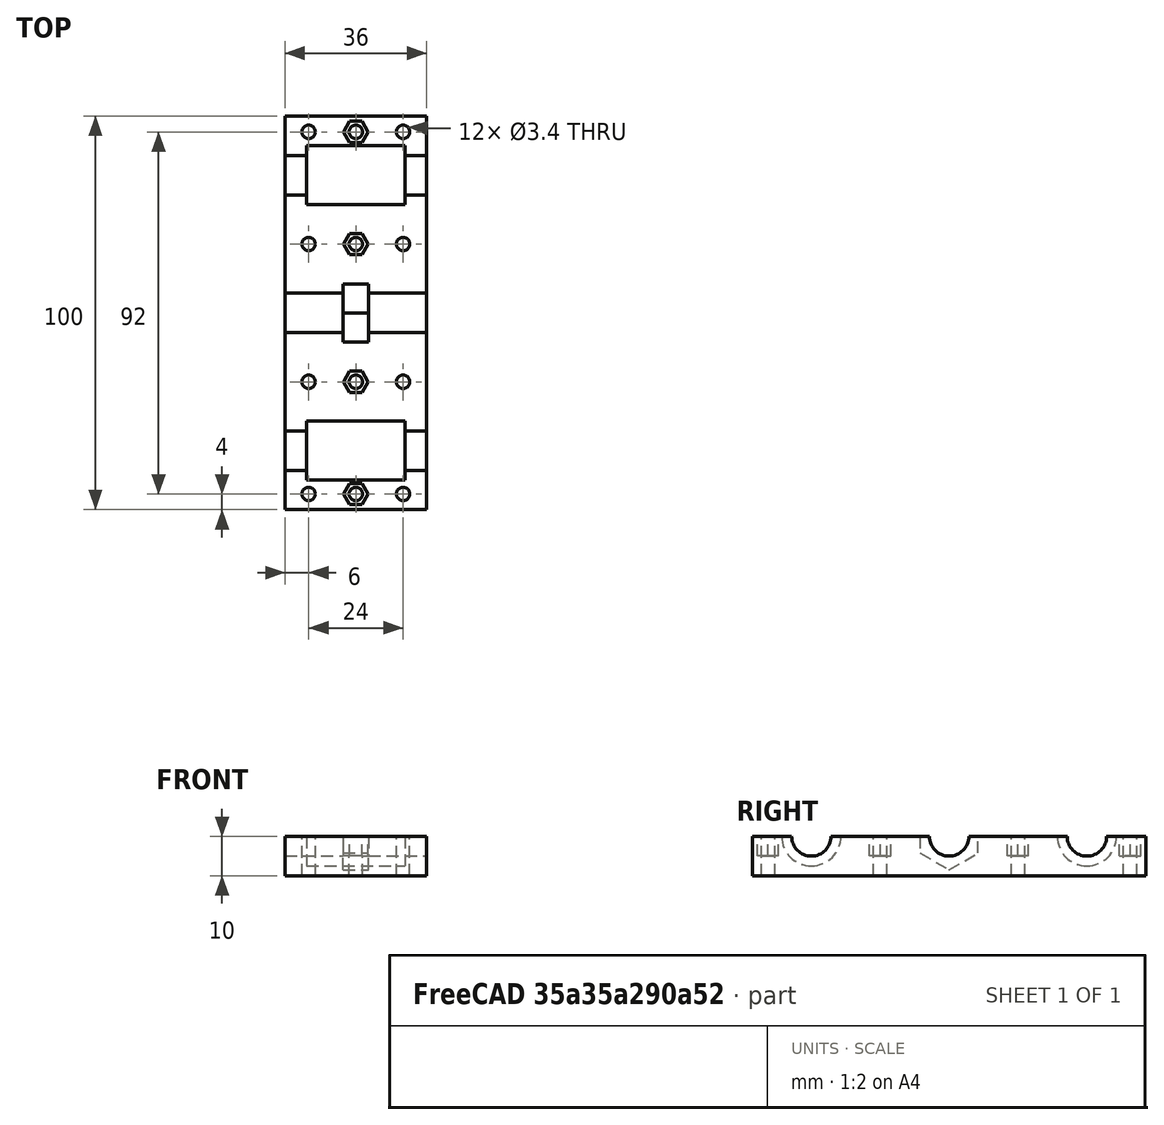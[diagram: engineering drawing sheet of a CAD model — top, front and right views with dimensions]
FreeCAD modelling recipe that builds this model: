
FCSTD DOCUMENT  (FreeCAD 0.14R3702 (Git))
Label: soporte_cabeza2
License: CC-BY 3.0
LicenseURL: http://creativecommons.org/licenses/by/3.0/
objects: Part::Cut×22, Part::Cylinder×17, Part::Prism×5, Part::Box×1
note: 45 computed .brp shape members not serialized (recipe doc carries the construction recipe); baked Part::Feature solids carry a one-line shape summary decoded from their .brp

FEATURE [Part::Box] Box  label="Cubo"
  Height = 10
  Length = 36
  Width = 100
FEATURE [Part::Cylinder] Cylinder  label="Cilindro"
  Angle = 360
  Height = 36
  Placement = pos=(0,15,10) rot=(0,1,0;1.5708rad)
  Radius = 5
FEATURE [Part::Cylinder] Cylinder001  label="Cilindro001"
  Angle = 360
  Height = 36
  Placement = pos=(0,50,10) rot=(0,1,0;1.5708rad)
  Radius = 5
FEATURE [Part::Cylinder] Cylinder002  label="Cilindro002"
  Angle = 360
  Height = 36
  Placement = pos=(0,85,10) rot=(0,1,0;1.5708rad)
  Radius = 5
FEATURE [Part::Cylinder] Cylinder003  label="Cilindro003"
  Angle = 360
  Height = 25
  Placement = pos=(5.5,15,10) rot=(0,1,0;1.5708rad)
  Radius = 7.5
FEATURE [Part::Cylinder] Cylinder004  label="Cilindro004"
  Angle = 360
  Height = 25
  Placement = pos=(5.5,85,10) rot=(0,1,0;1.5708rad)
  Radius = 7.5
FEATURE [Part::Prism] Prism  label="Prisma"
  Circumradius = 8.5
  Height = 6.5
  Placement = pos=(14.75,50,10) rot=(0,1,0;1.5708rad)
  Polygon = 6
FEATURE [Part::Cylinder] Cylinder005  label="Cilindro005"
  Angle = 360
  Height = 10
  Placement = pos=(6,4,0) rot=(0,0,1;0rad)
  Radius = 1.7
FEATURE [Part::Cylinder] Cylinder006  label="Cilindro006"
  Angle = 360
  Height = 10
  Placement = pos=(30,4,0) rot=(0,0,1;0rad)
  Radius = 1.7
FEATURE [Part::Cylinder] Cylinder007  label="Cilindro007"
  Angle = 360
  Height = 10
  Placement = pos=(6,32.5,0) rot=(0,0,1;0rad)
  Radius = 1.7
FEATURE [Part::Cylinder] Cylinder008  label="Cilindro008"
  Angle = 360
  Height = 10
  Placement = pos=(30,32.5,0) rot=(0,0,1;0rad)
  Radius = 1.7
FEATURE [Part::Cylinder] Cylinder009  label="Cilindro009"
  Angle = 360
  Height = 10
  Placement = pos=(6,67.5,0) rot=(0,0,1;0rad)
  Radius = 1.7
FEATURE [Part::Cylinder] Cylinder010  label="Cilindro010"
  Angle = 360
  Height = 10
  Placement = pos=(30,67.5,0) rot=(0,0,1;0rad)
  Radius = 1.7
FEATURE [Part::Cylinder] Cylinder011  label="Cilindro011"
  Angle = 360
  Height = 10
  Placement = pos=(6,96,0) rot=(0,0,1;0rad)
  Radius = 1.7
FEATURE [Part::Cylinder] Cylinder012  label="Cilindro012"
  Angle = 360
  Height = 10
  Placement = pos=(30,96,0) rot=(0,0,1;0rad)
  Radius = 1.7
FEATURE [Part::Prism] Prism001  label="Prisma001"
  Circumradius = 3.1
  Height = 5
  Placement = pos=(18,4,5) rot=(0,0,1;0rad)
  Polygon = 6
FEATURE [Part::Prism] Prism002  label="Prisma002"
  Circumradius = 3.1
  Height = 5
  Placement = pos=(18,32.5,5) rot=(0,0,1;0rad)
  Polygon = 6
FEATURE [Part::Prism] Prism003  label="Prisma003"
  Circumradius = 3.1
  Height = 5
  Placement = pos=(18,67.5,5) rot=(0,0,1;0rad)
  Polygon = 6
FEATURE [Part::Prism] Prism004  label="Prisma004"
  Circumradius = 3.1
  Height = 5
  Placement = pos=(18,96,5) rot=(0,0,1;0rad)
  Polygon = 6
FEATURE [Part::Cylinder] Cylinder013  label="Cilindro013"
  Angle = 360
  Height = 10
  Placement = pos=(18,4,0) rot=(0,0,1;0rad)
  Radius = 1.7
FEATURE [Part::Cylinder] Cylinder014  label="Cilindro014"
  Angle = 360
  Height = 10
  Placement = pos=(18,32.5,0) rot=(0,0,1;0rad)
  Radius = 1.7
FEATURE [Part::Cylinder] Cylinder015  label="Cilindro015"
  Angle = 360
  Height = 10
  Placement = pos=(18,67.5,0) rot=(0,0,1;0rad)
  Radius = 1.7
FEATURE [Part::Cylinder] Cylinder016  label="Cilindro016"
  Angle = 360
  Height = 10
  Placement = pos=(18,96,0) rot=(0,0,1;0rad)
  Radius = 1.7
FEATURE [Part::Cut] Cut
  Base = -> Box
  Tool = -> Cylinder
FEATURE [Part::Cut] Cut001
  Base = -> Cut
  Tool = -> Cylinder001
FEATURE [Part::Cut] Cut002
  Base = -> Cut001
  Tool = -> Cylinder002
FEATURE [Part::Cut] Cut003
  Base = -> Cut002
  Tool = -> Cylinder003
FEATURE [Part::Cut] Cut004
  Base = -> Cut003
  Tool = -> Cylinder004
FEATURE [Part::Cut] Cut005
  Base = -> Cut004
  Tool = -> Prism
FEATURE [Part::Cut] Cut006
  Base = -> Cut005
  Tool = -> Cylinder005
FEATURE [Part::Cut] Cut007
  Base = -> Cut006
  Tool = -> Cylinder006
FEATURE [Part::Cut] Cut008
  Base = -> Cut007
  Tool = -> Cylinder007
FEATURE [Part::Cut] Cut009
  Base = -> Cut008
  Tool = -> Cylinder008
FEATURE [Part::Cut] Cut010
  Base = -> Cut009
  Tool = -> Cylinder009
FEATURE [Part::Cut] Cut011
  Base = -> Cut010
  Tool = -> Cylinder010
FEATURE [Part::Cut] Cut012
  Base = -> Cut011
  Tool = -> Cylinder011
FEATURE [Part::Cut] Cut013
  Base = -> Cut012
  Tool = -> Cylinder012
FEATURE [Part::Cut] Cut014
  Base = -> Cut013
  Tool = -> Cylinder013
FEATURE [Part::Cut] Cut015
  Base = -> Cut014
  Tool = -> Cylinder014
FEATURE [Part::Cut] Cut016
  Base = -> Cut015
  Tool = -> Cylinder015
FEATURE [Part::Cut] Cut017
  Base = -> Cut016
  Tool = -> Cylinder016
FEATURE [Part::Cut] Cut018
  Base = -> Cut017
  Tool = -> Prism001
FEATURE [Part::Cut] Cut019
  Base = -> Cut018
  Tool = -> Prism002
FEATURE [Part::Cut] Cut020
  Base = -> Cut019
  Tool = -> Prism003
FEATURE [Part::Cut] Cut021
  Base = -> Cut020
  Tool = -> Prism004
